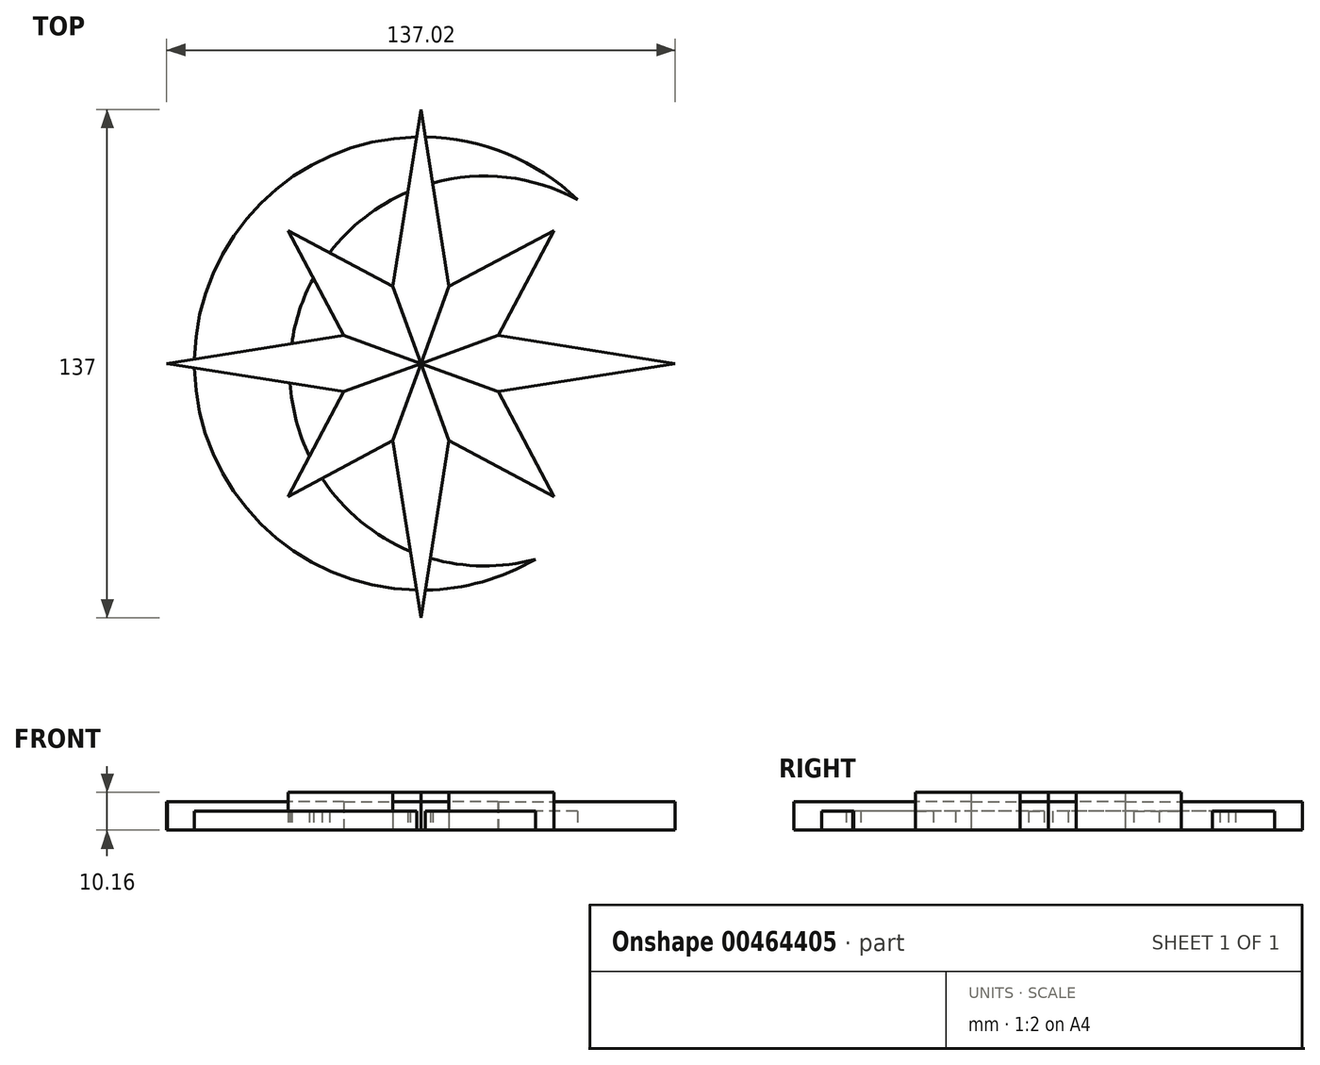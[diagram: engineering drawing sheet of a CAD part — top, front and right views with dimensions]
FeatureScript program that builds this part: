
annotation { "Feature Type Name" : "Feature", "Feature Type Description" : "" }
export const myFeature = defineFeature(function(context is Context, id is Id, definition is map)
    precondition{}
    {
        {
            var Q0;
            Q0=qCreatedBy(makeId("Top.planeOp"),FACE);
            var sketch = newSketch(context, id + "F0", { "sketchPlane" : qUnion([Q0])});
            skLineSegment(sketch, "E0", {"start": v(68.35, 0) * mm, "end": v(68.51, -0.03) * mm});
            skLineSegment(sketch, "E1.MirrorCS", {"start": v(-68.35, 0) * mm, "end": v(-68.51, 0.03) * mm});
            skLineSegment(sketch, "E2", {"start": v(68.51, 0.03) * mm, "end": v(68.51, -0.03) * mm});
            skLineSegment(sketch, "E3", {"start": v(-68.51, 0.03) * mm, "end": v(-68.51, -0.03) * mm});
            skPoint(sketch, "E4.orphan", {"position": v(0, -68.5) * mm});
            skLineSegment(sketch, "E5.trimOffspring", {"start": v(-68.35, 0) * mm, "end": v(-68.51, -0.03) * mm});
            skLineSegment(sketch, "E6.trimOffspring", {"start": v(68.35, 0) * mm, "end": v(68.51, 0.03) * mm});
            skPoint(sketch, "E7.MirrorCS.end.orphan", {"position": v(0, 68.5) * mm});
            skArc(sketch, "E8", {"start": v(42.12, 44.19) * mm, "mid": v(23.23, 56.45) * mm, "end": v(1.18, 61.04) * mm});
            skArc(sketch, "E9", {"start": v(42.12, 44.19) * mm, "mid": v(23.06, 50.17) * mm, "end": v(3.15, 48.6) * mm});
            skPoint(sketch, "E10.orphan", {"position": v(75.98, -68.5) * mm});
            skLineSegment(sketch, "E11", {"start": v(-7.56, 20.77) * mm, "end": v(0, 0) * mm});
            skLineSegment(sketch, "E12.MirrorCS", {"start": v(7.56, 20.77) * mm, "end": v(0, 0) * mm});
            skLineSegment(sketch, "E13.MirrorCS", {"start": v(-7.56, -20.77) * mm, "end": v(0, 0) * mm});
            skLineSegment(sketch, "E14.MirrorCS", {"start": v(7.56, -20.77) * mm, "end": v(0, 0) * mm});
            skLineSegment(sketch, "E15.MirrorCS", {"start": v(-20.78, 7.56) * mm, "end": v(0, 0) * mm});
            skLineSegment(sketch, "E16.MirrorCS", {"start": v(20.77, 7.57) * mm, "end": v(0, 0) * mm});
            skLineSegment(sketch, "E17.MirrorCS", {"start": v(20.77, -7.57) * mm, "end": v(0, 0) * mm});
            skLineSegment(sketch, "E18.MirrorCS", {"start": v(-20.78, -7.56) * mm, "end": v(0, 0) * mm});
            skLineSegment(sketch, "E19", {"start": v(-7.56, 20.77) * mm, "end": v(0, 68.5) * mm});
            skLineSegment(sketch, "E20", {"start": v(7.56, 20.77) * mm, "end": v(0, 68.5) * mm});
            skLineSegment(sketch, "E21", {"start": v(20.77, 7.57) * mm, "end": v(68.51, 0.03) * mm});
            skLineSegment(sketch, "E22", {"start": v(20.77, -7.57) * mm, "end": v(68.51, 0.03) * mm});
            skLineSegment(sketch, "E23", {"start": v(-7.56, -20.77) * mm, "end": v(0, -68.5) * mm});
            skLineSegment(sketch, "E24", {"start": v(7.56, -20.77) * mm, "end": v(0, -68.5) * mm});
            skLineSegment(sketch, "E25", {"start": v(-20.78, 7.56) * mm, "end": v(-68.51, 0.03) * mm});
            skLineSegment(sketch, "E26", {"start": v(-20.78, -7.56) * mm, "end": v(-68.35, 0) * mm});
            skLineSegment(sketch, "E27", {"start": v(-20.78, 7.56) * mm, "end": v(-35.82, 35.81) * mm});
            skLineSegment(sketch, "E28", {"start": v(-35.82, 35.81) * mm, "end": v(-7.56, 20.77) * mm});
            skLineSegment(sketch, "E29.MirrorCS", {"start": v(35.82, 35.81) * mm, "end": v(7.56, 20.77) * mm});
            skLineSegment(sketch, "E30.MirrorCS", {"start": v(20.78, 7.56) * mm, "end": v(35.82, 35.81) * mm});
            skLineSegment(sketch, "E31.MirrorCS", {"start": v(35.82, -35.81) * mm, "end": v(7.56, -20.77) * mm});
            skLineSegment(sketch, "E32.MirrorCS", {"start": v(20.78, -7.56) * mm, "end": v(35.82, -35.81) * mm});
            skLineSegment(sketch, "E33.MirrorCS", {"start": v(-20.78, -7.56) * mm, "end": v(-35.82, -35.81) * mm});
            skLineSegment(sketch, "E34.MirrorCS", {"start": v(-35.82, -35.81) * mm, "end": v(-7.56, -20.77) * mm});
            skPoint(sketch, "E35.orphan", {"position": v(68.51, -68.5) * mm});
            skPoint(sketch, "E36.start.orphan", {"position": v(22.1, 0) * mm});
            skPoint(sketch, "E37.start.orphan", {"position": v(0, -22.1) * mm});
            skPoint(sketch, "E38.start.orphan", {"position": v(-22.1, 0.03) * mm});
            skPoint(sketch, "E39.start.orphan", {"position": v(0, 22.1) * mm});
            skArc(sketch, "E40.trimOffspring", {"start": v(2.55, -52.42) * mm, "mid": v(16.69, -54.49) * mm, "end": v(30.86, -52.67) * mm});
            skArc(sketch, "E41.trimOffspring", {"start": v(1.18, -61.04) * mm, "mid": v(16.56, -58.76) * mm, "end": v(30.86, -52.67) * mm});
            skArc(sketch, "E42.trimOffspring", {"start": v(-26.65, -30.93) * mm, "mid": v(-16.22, -42.52) * mm, "end": v(-2.85, -50.53) * mm});
            skArc(sketch, "E43.trimOffspring", {"start": v(-35.24, -5.26) * mm, "mid": v(-33.6, -15.37) * mm, "end": v(-30.05, -24.97) * mm});
            skArc(sketch, "E44.trimOffspring", {"start": v(-61.04, -1.16) * mm, "mid": v(-43.17, -43.16) * mm, "end": v(-1.18, -61.04) * mm});
            skArc(sketch, "E45.trimOffspring", {"start": v(-29, 23) * mm, "mid": v(-32.7, 14.44) * mm, "end": v(-34.83, 5.34) * mm});
            skArc(sketch, "E46.trimOffspring", {"start": v(-3.52, 46.26) * mm, "mid": v(-15.12, 39.4) * mm, "end": v(-24.6, 29.84) * mm});
            skArc(sketch, "E47.trimOffspring", {"start": v(-1.18, 61.04) * mm, "mid": v(-43.16, 43.18) * mm, "end": v(-61.04, 1.21) * mm});
            skArc(sketch, "E48.trimOffspring", {"start": v(20.78, 7.56) * mm, "mid": v(20.77, 7.56) * mm, "end": v(20.77, 7.57) * mm});
            skArc(sketch, "E49.trimOffspring", {"start": v(20.77, -7.57) * mm, "mid": v(20.77, -7.56) * mm, "end": v(20.78, -7.56) * mm});
            skSolve(sketch);
        }
        {
            var Q0;
            {var subQ0=sQuery(id+"F0.wireOp",EDGE,"E8");Q0=makeQuery(id+"F0.imprint","IMPRINT",FACE,{"disambiguationData":[TD([[makeQuery(id+"F0.imprint","IMPRINT",EDGE,{"derivedFrom":subQ0}),1.0]])]});}
            var Q1;
            {var subQ4=sQuery(id+"F0.wireOp",EDGE,"E45.trimOffspring");Q1=makeQuery(id+"F0.imprint","IMPRINT",FACE,{"disambiguationData":[TD([[makeQuery(id+"F0.imprint","IMPRINT",EDGE,{"derivedFrom":subQ4}),-1.0]])]});}
            var Q2;
            {var subQ3=sQuery(id+"F0.wireOp",EDGE,"E42.trimOffspring");Q2=makeQuery(id+"F0.imprint","IMPRINT",FACE,{"disambiguationData":[TD([[makeQuery(id+"F0.imprint","IMPRINT",EDGE,{"derivedFrom":subQ3}),-1.0]])]});}
            var Q3;
            {var subQ0=sQuery(id+"F0.wireOp",EDGE,"E40.trimOffspring");Q3=makeQuery(id+"F0.imprint","IMPRINT",FACE,{"disambiguationData":[TD([[makeQuery(id+"F0.imprint","IMPRINT",EDGE,{"derivedFrom":subQ0}),-1.0]])]});}
            extrude(context, id + "F1", {"entities" : qUnion([Q0, Q1, Q2, Q3]), "depth" : 5.08 * mm});
        }
        {
            var Q0;
            {var subQ2=sQuery(id+"F0.wireOp",EDGE,"E1.MirrorCS");Q0=makeQuery(id+"F0.imprint","IMPRINT",FACE,{"disambiguationData":[TD([[makeQuery(id+"F0.imprint","IMPRINT",EDGE,{"derivedFrom":subQ2}),-1.0]])]});}
            var Q1;
            {var subQ3=sQuery(id+"F0.wireOp",EDGE,"E11");Q1=makeQuery(id+"F0.imprint","IMPRINT",FACE,{"disambiguationData":[TD([[makeQuery(id+"F0.imprint","IMPRINT",EDGE,{"derivedFrom":subQ3}),1.0]])]});}
            var Q2;
            Q2=makeQuery(id+"F0.imprint","IMPRINT",FACE,{"disambiguationData":[TD([[makeQuery(id+"F0.imprint","IMPRINT",EDGE,{"derivedFrom":sQuery(id+"F0.wireOp",EDGE,"E16.MirrorCS")}),1.0]])]});
            var Q3;
            {var subQ3=sQuery(id+"F0.wireOp",EDGE,"E13.MirrorCS");Q3=makeQuery(id+"F0.imprint","IMPRINT",FACE,{"disambiguationData":[TD([[makeQuery(id+"F0.imprint","IMPRINT",EDGE,{"derivedFrom":subQ3}),-1.0]])]});}
            extrude(context, id + "F2", {"entities" : qUnion([Q0, Q1, Q2, Q3]), "depth" : 7.62 * mm});
        }
        {
            var Q0;
            {var subQ5=sQuery(id+"F0.wireOp",EDGE,"E11");Q0=makeQuery(id+"F0.imprint","IMPRINT",FACE,{"disambiguationData":[TD([[makeQuery(id+"F0.imprint","IMPRINT",EDGE,{"derivedFrom":subQ5}),-1.0]])]});}
            var Q1;
            Q1=makeQuery(id+"F0.imprint","IMPRINT",FACE,{"disambiguationData":[TD([[makeQuery(id+"F0.imprint","IMPRINT",EDGE,{"derivedFrom":sQuery(id+"F0.wireOp",EDGE,"E12.MirrorCS")}),1.0]])]});
            var Q2;
            Q2=makeQuery(id+"F0.imprint","IMPRINT",FACE,{"disambiguationData":[TD([[makeQuery(id+"F0.imprint","IMPRINT",EDGE,{"derivedFrom":sQuery(id+"F0.wireOp",EDGE,"E14.MirrorCS")}),-1.0]])]});
            var Q3;
            {var subQ5=sQuery(id+"F0.wireOp",EDGE,"E13.MirrorCS");Q3=makeQuery(id+"F0.imprint","IMPRINT",FACE,{"disambiguationData":[TD([[makeQuery(id+"F0.imprint","IMPRINT",EDGE,{"derivedFrom":subQ5}),1.0]])]});}
            extrude(context, id + "F3", {"entities" : qUnion([Q0, Q1, Q2, Q3]), "depth" : 10.16 * mm});
        }
    });
